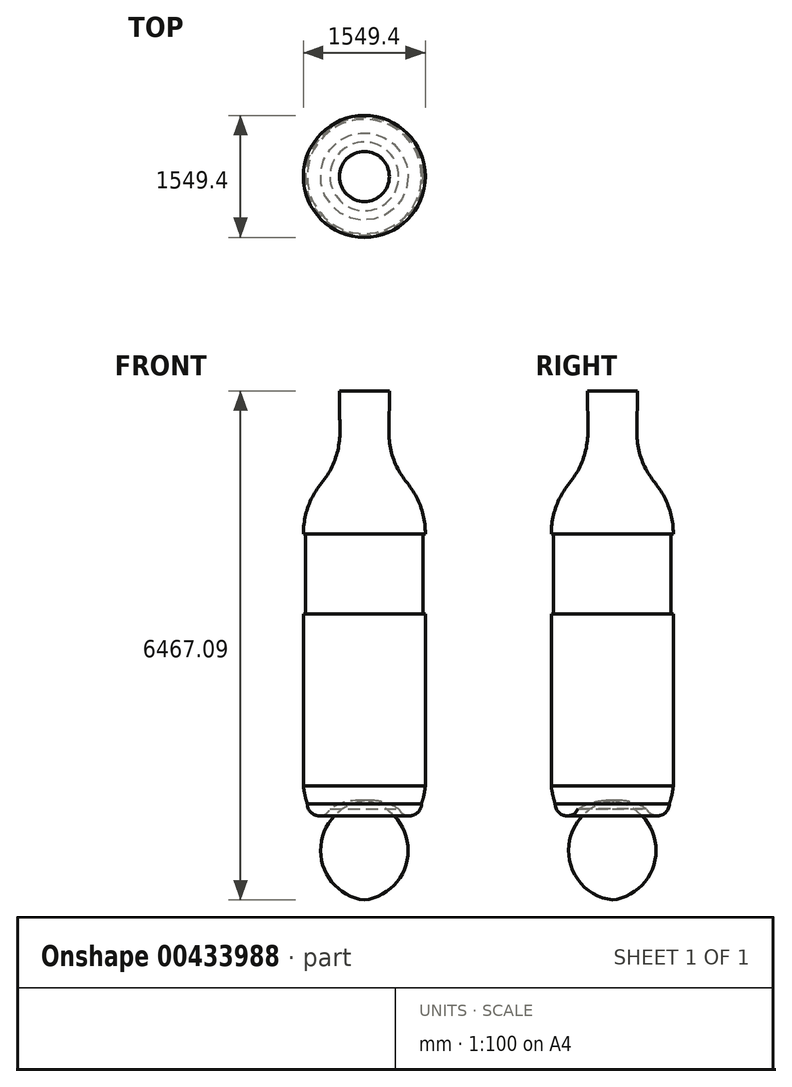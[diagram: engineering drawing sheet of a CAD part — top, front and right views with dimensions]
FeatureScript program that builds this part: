
annotation { "Feature Type Name" : "Feature", "Feature Type Description" : "" }
export const myFeature = defineFeature(function(context is Context, id is Id, definition is map)
    precondition{}
    {
        {
            var Q0;
            Q0=qCreatedBy(makeId("Front.planeOp"),FACE);
            var sketch = newSketch(context, id + "F0", { "sketchPlane" : qUnion([Q0])});
            skLineSegment(sketch, "E0", {"start": v(-1589.26, 1218.16) * mm, "end": v(-1589.26, 3407.1) * mm});
            skLineSegment(sketch, "E1", {"start": v(-814.56, 6237.17) * mm, "end": v(-1132.06, 6237.17) * mm});
            skLineSegment(sketch, "E2", {"start": v(-1132.06, 6237.17) * mm, "end": v(-1125.27, 5729.21) * mm});
            skArc(sketch, "E3", {"start": v(-1359.45, 5066.66) * mm, "mid": v(-1183.25, 5377.04) * mm, "end": v(-1125.27, 5729.21) * mm});
            skArc(sketch, "E4", {"start": v(-1359.45, 5066.66) * mm, "mid": v(-1530.09, 4764.78) * mm, "end": v(-1589.26, 4423.1) * mm});
            skArc(sketch, "E5", {"start": v(-1540.17, 992.07) * mm, "mid": v(-1422.07, 843.58) * mm, "end": v(-1250.8, 925.23) * mm});
            skArc(sketch, "E6", {"start": v(-1589.26, 1474.67) * mm, "mid": v(-1590.61, 1230.73) * mm, "end": v(-1540.17, 992.07) * mm});
            skArc(sketch, "E7", {"start": v(-814.56, 1030.17) * mm, "mid": v(-1042.26, 1017.51) * mm, "end": v(-1250.8, 925.23) * mm});
            skPoint(sketch, "E8.orphan", {"position": v(-1589.26, 839.67) * mm});
            skPoint(sketch, "E9.orphan", {"position": v(-814.56, 839.67) * mm});
            skLineSegment(sketch, "E10", {"start": v(-1561.32, 4423.1) * mm, "end": v(-1561.32, 3407.1) * mm});
            skLineSegment(sketch, "E11", {"start": v(-1561.32, 4423.1) * mm, "end": v(-1589.26, 4423.1) * mm});
            skLineSegment(sketch, "E12", {"start": v(-1561.32, 3407.1) * mm, "end": v(-1589.26, 3407.1) * mm});
            skLineSegment(sketch, "E13.MirrorCS", {"start": v(-67.8, 4423.1) * mm, "end": v(-39.86, 4423.1) * mm});
            skLineSegment(sketch, "E14.MirrorCS", {"start": v(-67.8, 3407.1) * mm, "end": v(-39.86, 3407.1) * mm});
            skLineSegment(sketch, "E15", {"start": v(-814.56, 1030.17) * mm, "end": v(-814.56, 6237.17) * mm});
            skSolve(sketch);
        }
        {
            var Q0;
            Q0=makeQuery(id+"F0.imprint","IMPRINT",FACE,{"disambiguationData":[TD([[makeQuery(id+"F0.imprint","IMPRINT",EDGE,{"derivedFrom":sQuery(id+"F0.wireOp",EDGE,"E1")}),1.0]])]});
            var Q1;
            Q1=sQuery(id+"F0.wireOp",EDGE,"E15");
            revolve(context, id + "F1", {"entities" : qUnion([Q0]), "axis" : qUnion([Q1]), "revolveType" : RevolveType.FULL});
        }
    });
